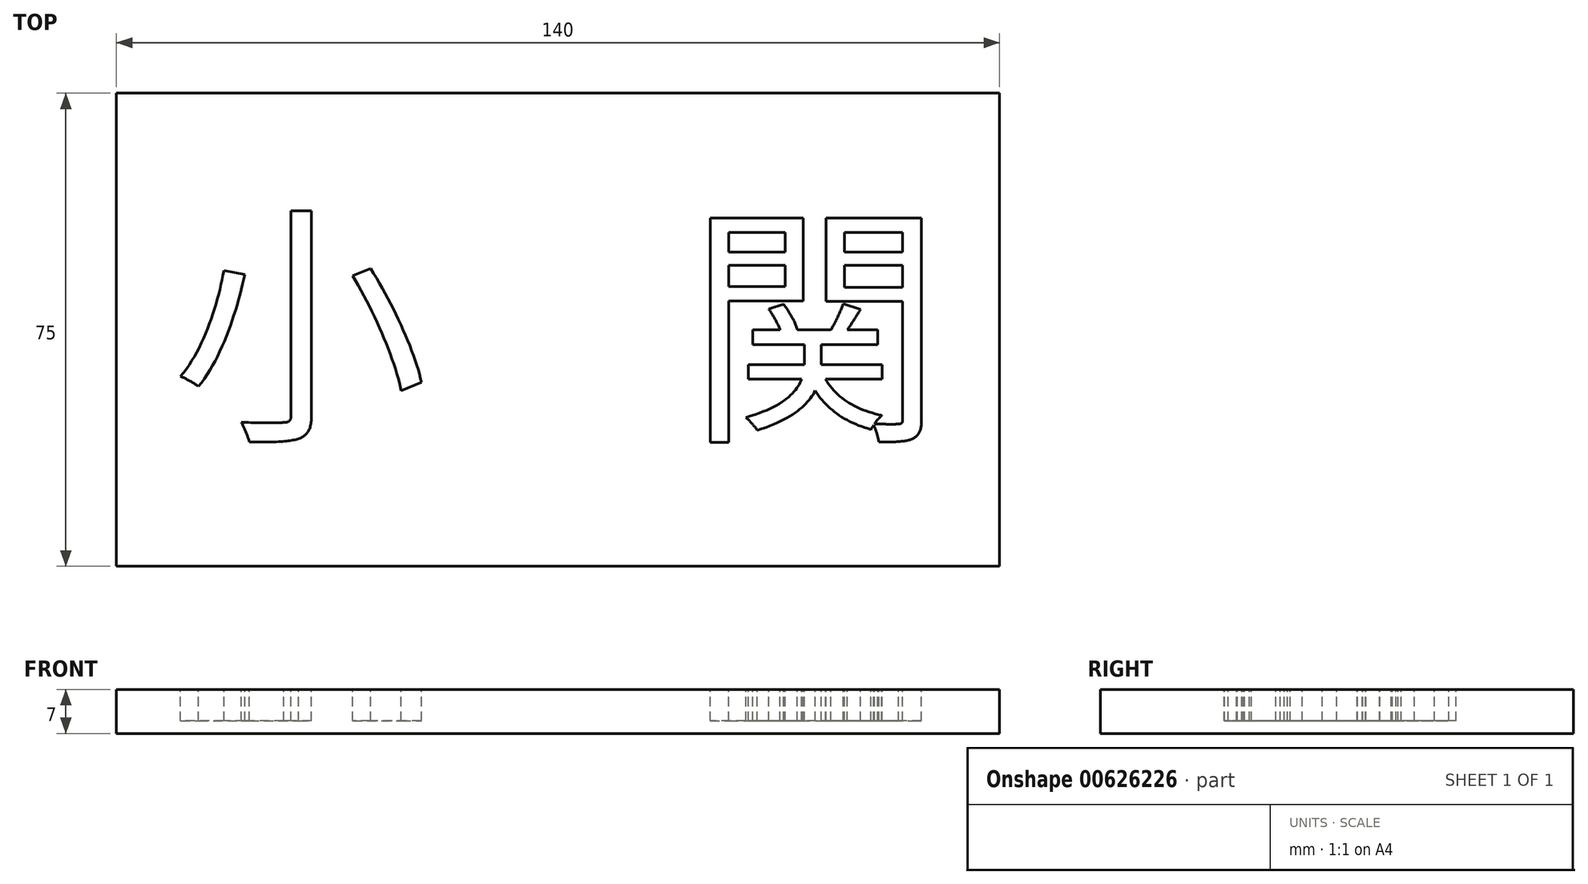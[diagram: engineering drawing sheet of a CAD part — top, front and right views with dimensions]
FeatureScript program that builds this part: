
annotation { "Feature Type Name" : "Feature", "Feature Type Description" : "" }
export const myFeature = defineFeature(function(context is Context, id is Id, definition is map)
    precondition{}
    {
        {
            var Q0;
            Q0=qCreatedBy(makeId("Top.planeOp"),FACE);
            var sketch = newSketch(context, id + "F0", { "sketchPlane" : qUnion([Q0])});
            skLineSegment(sketch, "E0.bottom", {"start": v(-70, 37.5) * mm, "end": v(70, 37.5) * mm});
            skLineSegment(sketch, "E0.top", {"start": v(-70, -37.5) * mm, "end": v(70, -37.5) * mm});
            skLineSegment(sketch, "E0.left", {"start": v(-70, 37.5) * mm, "end": v(-70, -37.5) * mm});
            skLineSegment(sketch, "E0.right", {"start": v(70, 37.5) * mm, "end": v(70, -37.5) * mm});
            skSolve(sketch);
        }
        {
            var Q0;
            Q0=makeQuery(id+"F0.imprint","IMPRINT",FACE,{"disambiguationData":[TD([[makeQuery(id+"F0.imprint","IMPRINT",EDGE,{"derivedFrom":sQuery(id+"F0.wireOp",EDGE,"E0.bottom")}),-1.0]])]});
            extrude(context, id + "F1", {"entities" : qUnion([Q0]), "depth" : 7 * mm, "offsetDistance" : 25 * mm});
        }
        {
            var Q0;
            Q0=makeQuery(id+"F1.opExtrude","CAP_FACE",FACE,{"disambiguationData":[OSD([sQuery(id+"F0.wireOp",EDGE,"E0.bottom"),sQuery(id+"F0.wireOp",EDGE,"E0.top"),sQuery(id+"F0.wireOp",EDGE,"E0.left"),sQuery(id+"F0.wireOp",EDGE,"E0.right")])],"isStart":false});
            var sketch = newSketch(context, id + "F2", { "sketchPlane" : qUnion([Q0])});
            skText(sketch, "E1", { "text": "小　関", "fontName": "NotoSansCJKjp-Regular.otf"});
            const initialGuessF2  = {"E1": [-0.0613, -0.0147, 1, 0, 0.0294]};
            skSetInitialGuess(sketch, initialGuessF2);
            skSolve(sketch);
        }
        {
            var Q0;
            Q0 = qSketchRegion(id + "F2", true);
            extrude(context, id + "F3", {"entities" : qUnion([Q0]), "operationType" : NewBodyOperationType.REMOVE, "oppositeDirection" : true, "depth" : 5 * mm, "offsetDistance" : 25 * mm});
        }
    });
